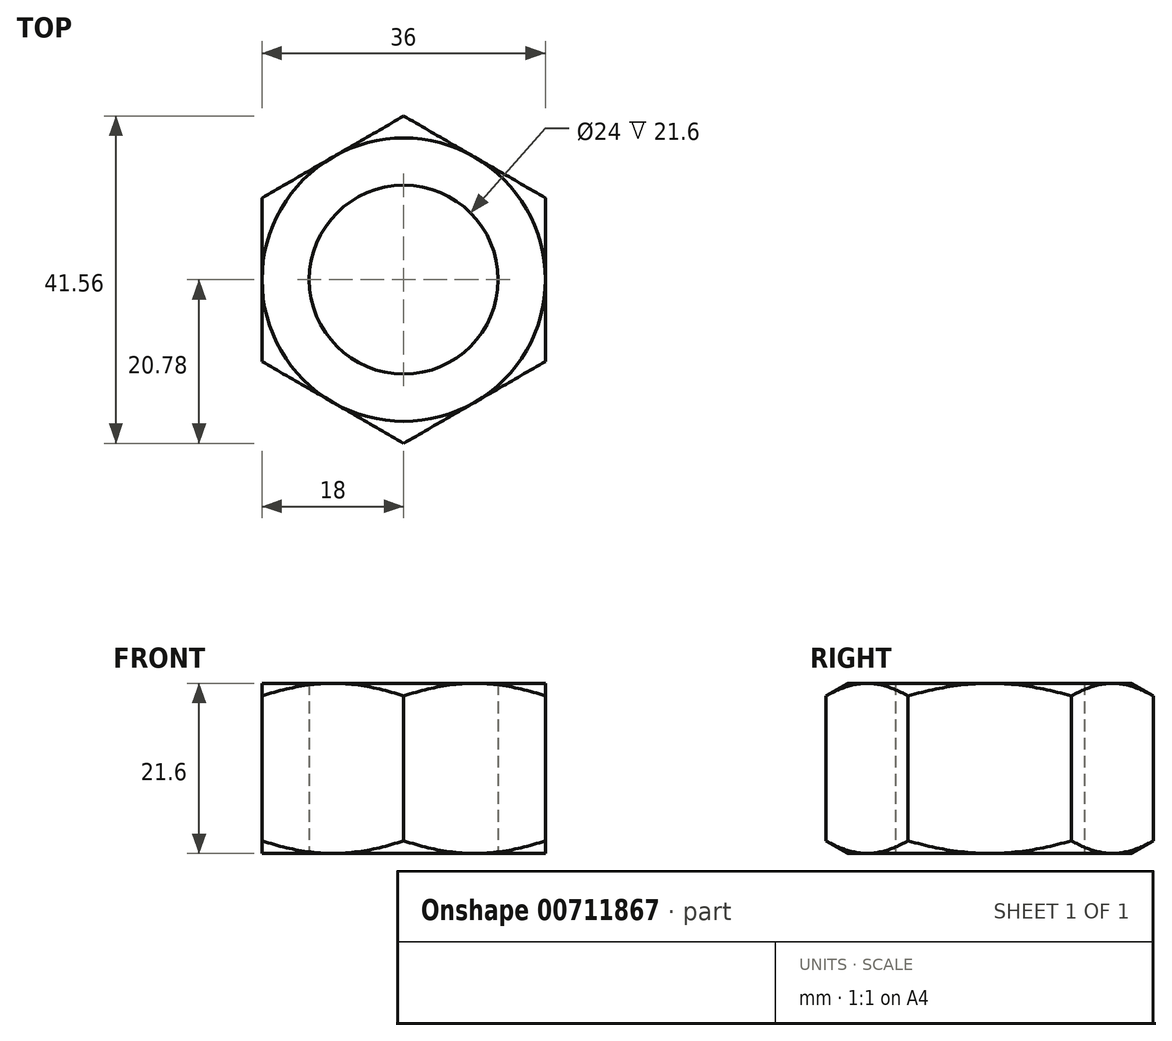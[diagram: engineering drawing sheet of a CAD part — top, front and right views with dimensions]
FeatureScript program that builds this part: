
annotation { "Feature Type Name" : "Feature", "Feature Type Description" : "" }
export const myFeature = defineFeature(function(context is Context, id is Id, definition is map)
    precondition{}
    {
        {
            var Q0;
            Q0=qCreatedBy(makeId("Top.planeOp"),FACE);
            var sketch = newSketch(context, id + "F0", { "sketchPlane" : qUnion([Q0])});
            skCircle(sketch, "E0.cCircle", {"center": v(0, 0) * mm, "radius": 18 * mm, "construction": true});
            skLineSegment(sketch, "E0.0", {"start": v(0, 20.78) * mm, "end": v(18, 10.4) * mm});
            skLineSegment(sketch, "E0.1", {"start": v(18, 10.4) * mm, "end": v(18, -10.4) * mm});
            skLineSegment(sketch, "E0.2", {"start": v(18, -10.4) * mm, "end": v(0, -20.78) * mm});
            skLineSegment(sketch, "E0.3", {"start": v(0, -20.78) * mm, "end": v(-18, -10.4) * mm});
            skLineSegment(sketch, "E0.4", {"start": v(-18, -10.4) * mm, "end": v(-18, 10.4) * mm});
            skLineSegment(sketch, "E0.5", {"start": v(-18, 10.4) * mm, "end": v(0, 20.78) * mm});
            skPoint(sketch, "E0.0.midPoint", {"position": v(9, 15.59) * mm});
            skCircle(sketch, "E1", {"center": v(0, 0) * mm, "radius": 12 * mm});
            skSolve(sketch);
        }
        {
            var Q0;
            Q0 = qSketchRegion(id + "F0", true);
            extrude(context, id + "F1", {"entities" : qUnion([Q0]), "depth" : 21.6 * mm, "offsetDistance" : 25 * mm});
        }
        {
            var Q0;
            Q0=qCreatedBy(makeId("Front.planeOp"),FACE);
            var sketch = newSketch(context, id + "F2", { "sketchPlane" : qUnion([Q0])});
            skLineSegment(sketch, "E2", {"start": v(0, 0) * mm, "end": v(0, 21.6) * mm});
            skLineSegment(sketch, "E3", {"start": v(0, 10.8) * mm, "end": v(17.1, 10.8) * mm, "construction": true});
            skLineSegment(sketch, "E4", {"start": v(18, 21.6) * mm, "end": v(27, 21.6) * mm});
            skLineSegment(sketch, "E5", {"start": v(27, 21.6) * mm, "end": v(27, 16.4) * mm});
            skLineSegment(sketch, "E6", {"start": v(27, 16.4) * mm, "end": v(18, 21.6) * mm});
            skLineSegment(sketch, "E7.MirrorCS", {"start": v(18, 0) * mm, "end": v(27, 0) * mm});
            skLineSegment(sketch, "E8.MirrorCS", {"start": v(27, 5.2) * mm, "end": v(18, 0) * mm});
            skLineSegment(sketch, "E9.MirrorCS", {"start": v(27, 0) * mm, "end": v(27, 5.2) * mm});
            skSolve(sketch);
        }
        {
            var Q0;
            Q0 = qSketchRegion(id + "F2", true);
            var Q1;
            Q1=sQuery(id+"F2.wireOp",EDGE,"E2");
            revolve(context, id + "F3", {"operationType" : NewBodyOperationType.REMOVE, "surfaceOperationType" : NewSurfaceOperationType.NEW, "entities" : qUnion([Q0]), "axis" : qUnion([Q1]), "revolveType" : RevolveType.FULL, "oppositeDirection" : true});
        }
    });
